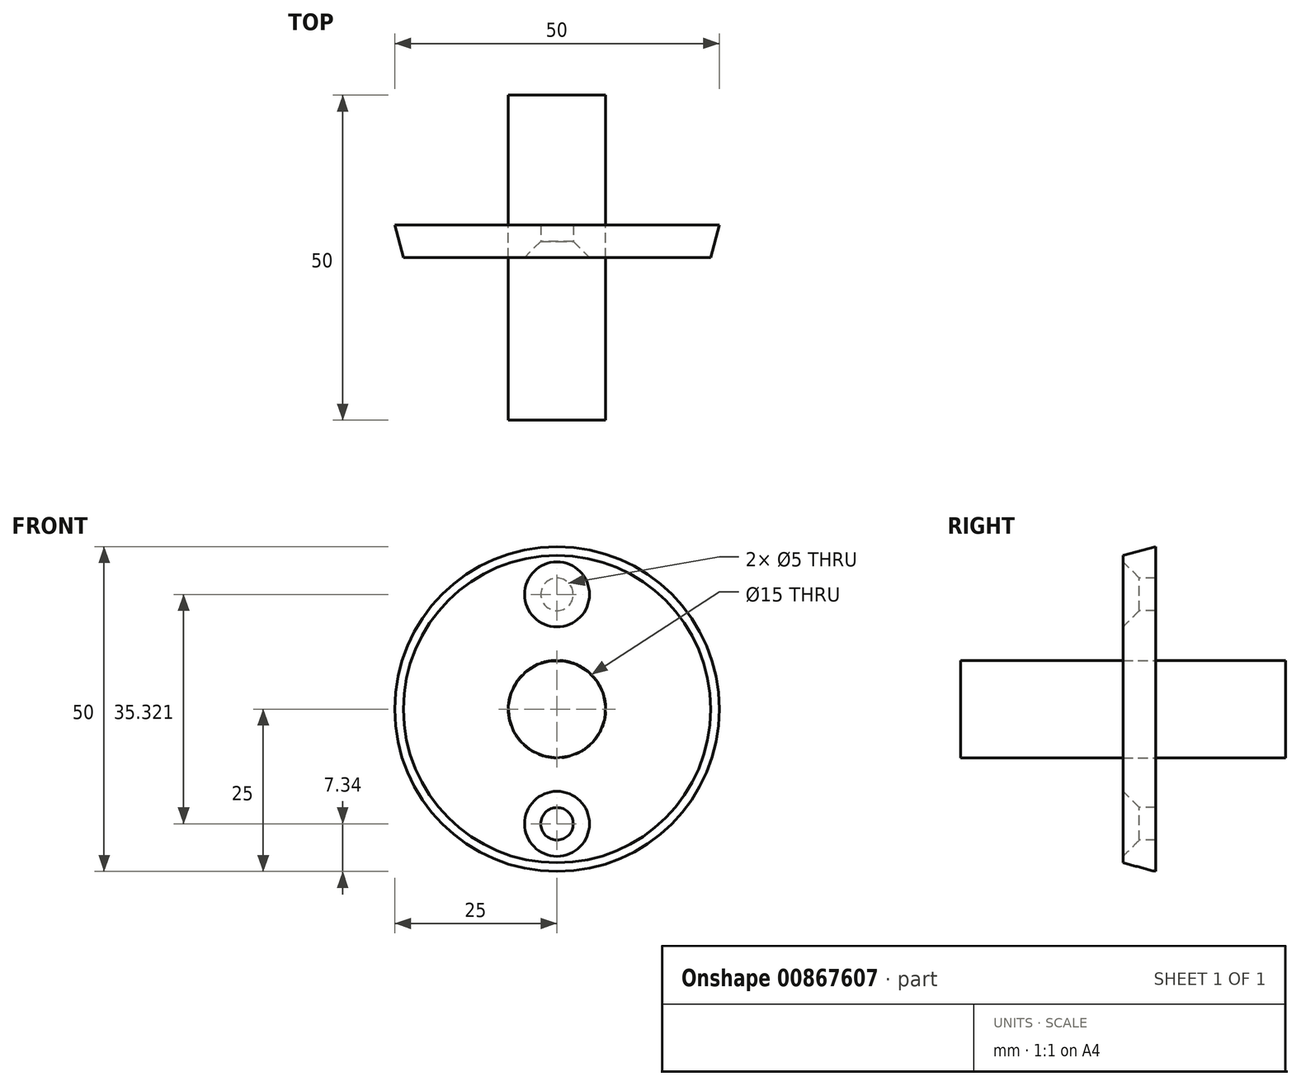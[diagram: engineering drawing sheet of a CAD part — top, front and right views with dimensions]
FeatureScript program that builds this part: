
annotation { "Feature Type Name" : "Feature", "Feature Type Description" : "" }
export const myFeature = defineFeature(function(context is Context, id is Id, definition is map)
    precondition{}
    {
        {
            var Q0;
            Q0=qCreatedBy(makeId("Front.planeOp"),FACE);
            var sketch = newSketch(context, id + "F0", { "sketchPlane" : qUnion([Q0])});
            skCircle(sketch, "E0", {"center": v(0, 0) * mm, "radius": 25 * mm});
            skSolve(sketch);
        }
        {
            var Q0;
            Q0=makeQuery(id+"F0.imprint","IMPRINT",FACE,{"disambiguationData":[TD([[makeQuery(id+"F0.imprint","IMPRINT",EDGE,{"derivedFrom":sQuery(id+"F0.wireOp",EDGE,"E0")}),1.0]])]});
            extrude(context, id + "F1", {"entities" : qUnion([Q0]), "depth" : 5 * mm, "offsetDistance" : 25 * mm, "hasDraft" : true, "draftAngle" : 15 * degree, "draftPullDirection" : true});
        }
        {
            var Q0;
            Q0=makeQuery(id+"F1.opExtrude","CAP_FACE",FACE,{"disambiguationData":[OSD([sQuery(id+"F0.wireOp",EDGE,"E0")])],"isStart":false});
            var sketch = newSketch(context, id + "F2", { "sketchPlane" : qUnion([Q0])});
            skPoint(sketch, "E1", {"position": v(0, 17.66) * mm});
            skPoint(sketch, "E2.MirrorP", {"position": v(0, -17.66) * mm});
            skSolve(sketch);
        }
        {
            var Q0;
            Q0=sQuery(id+"F2.wireOp",VERTEX,"E1");
            var Q1;
            Q1=sQuery(id+"F2.wireOp",VERTEX,"E2.MirrorP");
            var Q2;
            Q2=makeQuery(id+"F1.opExtrude","SWEPT_BODY",BODY,{"disambiguationData":[OSD([sQuery(id+"F0.wireOp",EDGE,"E0")])]});
            hole(context, id + "F3", {"style" : HoleStyle.C_SINK, "endStyle" : HoleEndStyle.BLIND, "holeDiameter" : 5 * mm, "cSinkDiameter" : 10 * mm, "cSinkAngle" : 90 * degree, "majorDiameter" : 5 * mm, "holeDepth" : 12 * mm, "isTappedThrough" : true, "tappedDepth" : 12 * mm, "tapClearance" : 3, "startFromSketch" : true, "locations" : qUnion([Q0, Q1]), "scope" : qUnion([Q2])});
        }
        {
            var Q0;
            Q0=makeQuery(id+"F1.opExtrude","CAP_FACE",FACE,{"disambiguationData":[OSD([sQuery(id+"F0.wireOp",EDGE,"E0")])],"isStart":false});
            var sketch = newSketch(context, id + "F4", { "sketchPlane" : qUnion([Q0])});
            skCircle(sketch, "E3", {"center": v(0, 0) * mm, "radius": 7.5 * mm});
            skSolve(sketch);
        }
        {
            var Q0;
            Q0 = qSketchRegion(id + "F4", true);
            extrude(context, id + "F5", {"entities" : qUnion([Q0]), "endBound" : BoundingType.SYMMETRIC, "depth" : 50 * mm, "offsetDistance" : 25 * mm});
        }
        {
            var Q0;
            Q0=makeQuery(id+"F5.opExtrude","SWEPT_BODY",BODY,{"disambiguationData":[OSD([sQuery(id+"F4.wireOp",EDGE,"E3")])]});
            var Q1;
            Q1=makeQuery(id+"F1.opExtrude","SWEPT_BODY",BODY,{"disambiguationData":[OSD([sQuery(id+"F0.wireOp",EDGE,"E0")])]});
            booleanBodies(context, id + "F6", {"operationType" : BooleanOperationType.SUBTRACTION, "tools" : qUnion([Q0]), "targets" : qUnion([Q1]), "keepTools" : true});
        }
        {
            var Q0;
            Q0=makeQuery(id+"F5.opExtrude","CAP_FACE",FACE,{"disambiguationData":[OSD([sQuery(id+"F4.wireOp",EDGE,"E3")])],"isStart":false});
            var sketch = newSketch(context, id + "F7", { "sketchPlane" : qUnion([Q0])});
            skFitSpline(sketch, "E4", {"points": [v(0, 7.5) * mm, v(-80.92, 3.9) * mm, v(0, -7.5) * mm], "startDerivative": vector(-245.63, 4.91) * mm, "endDerivative": vector(245.74, -2.33) * mm});
            skSolve(sketch);
        }
        {
            var Q0;
            {var subQ0=sQuery(id+"F7.wireOp",EDGE,"E4");var subQ1=makeQuery(id+"F5.opExtrude","CAP_EDGE",EDGE,{"disambiguationData":[OSD([sQuery(id+"F4.wireOp",EDGE,"E3")])],"isStart":false});var subQ2=makeQuery(id+"F7.imprint","INTERSECT",VERTEX,{"disambiguationData":[OD(0.0)],"derivedFrom":[subQ1,subQ0]});Q0=makeQuery(id+"F7.imprint","IMPRINT",FACE,{"disambiguationData":[TD([[makeQuery(id+"F7.imprint","IMPRINT",EDGE,{"disambiguationData":[TD([[subQ2,-1.0]])],"derivedFrom":subQ0}),1.0]])]});}
            extrude(context, id + "F8", {"entities" : qUnion([Q0]), "operationType" : NewBodyOperationType.ADD, "oppositeDirection" : true, "depth" : 10 * mm, "offsetDistance" : 25 * mm});
        }
        {
            var Q0;
            Q0=makeQuery(id+"F1.opExtrude","CAP_FACE",FACE,{"disambiguationData":[OSD([sQuery(id+"F0.wireOp",EDGE,"E0")])],"isStart":false});
            var sketch = newSketch(context, id + "F9", { "sketchPlane" : qUnion([Q0])});
            skCircle(sketch, "E5.0", {"center": v(0, 17.66) * mm, "radius": 5 * mm});
            skSolve(sketch);
        }
        {
            var Q0;
            Q0 = qSketchRegion(id + "F9", true);
            var Q1;
            Q1=makeQuery(id+"F1.opExtrude","CAP_FACE",FACE,{"disambiguationData":[OSD([sQuery(id+"F0.wireOp",EDGE,"E0")])],"isStart":true});
            extrude(context, id + "F10", {"entities" : qUnion([Q0]), "endBound" : BoundingType.UP_TO_SURFACE, "oppositeDirection" : true, "depth" : 25 * mm, "endBoundEntityFace" : qUnion([Q1]), "offsetDistance" : 25 * mm});
        }
        {
            var Q0;
            Q0=makeQuery(id+"F1.opExtrude","SWEPT_BODY",BODY,{"disambiguationData":[OSD([sQuery(id+"F0.wireOp",EDGE,"E0")])]});
            var Q1;
            Q1=makeQuery(id+"F10.opExtrude","SWEPT_BODY",BODY,{"disambiguationData":[OSD([sQuery(id+"F9.wireOp",EDGE,"E5.0")])]});
            booleanBodies(context, id + "F11", {"operationType" : BooleanOperationType.SUBTRACTION, "tools" : qUnion([Q0]), "targets" : qUnion([Q1]), "keepTools" : true});
        }
    });
